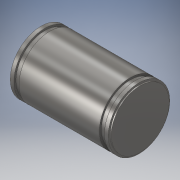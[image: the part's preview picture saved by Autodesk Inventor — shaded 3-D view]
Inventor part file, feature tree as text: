
AUTODESK INVENTOR PART (.ipt)
format: ipt  version: 2018 (Build 220112000, 112)  size: 148,480 bytes
history: native  units: in
note: dims shown in document units (in); Inventor stores cm internally (conversion verified against a paired STEP export)
features: revolve x1, sketch x1
ambient origin geometry x8: Origin, YZ Plane, XZ Plane, XY Plane, X Axis, Y Axis, Z Axis, Center Point
bodies: Solid1 (feature_tree)
feature tree (2):
  revolve  "Revolution1"  [1 undecoded]
  sketch  "Sketch1"  dims[d0=36.0in d1=98.0in d3=6.0in d4=2.0in d5=2.0in d6=4.0in d7=90.0deg d8=8.0in d9=92.0in d10=128.0in]
note: 1 required parameter value undecoded (feature->parameter linkage not recoverable at this tier; creation-order binding heuristic only, values carry confidence <= 0.55)
